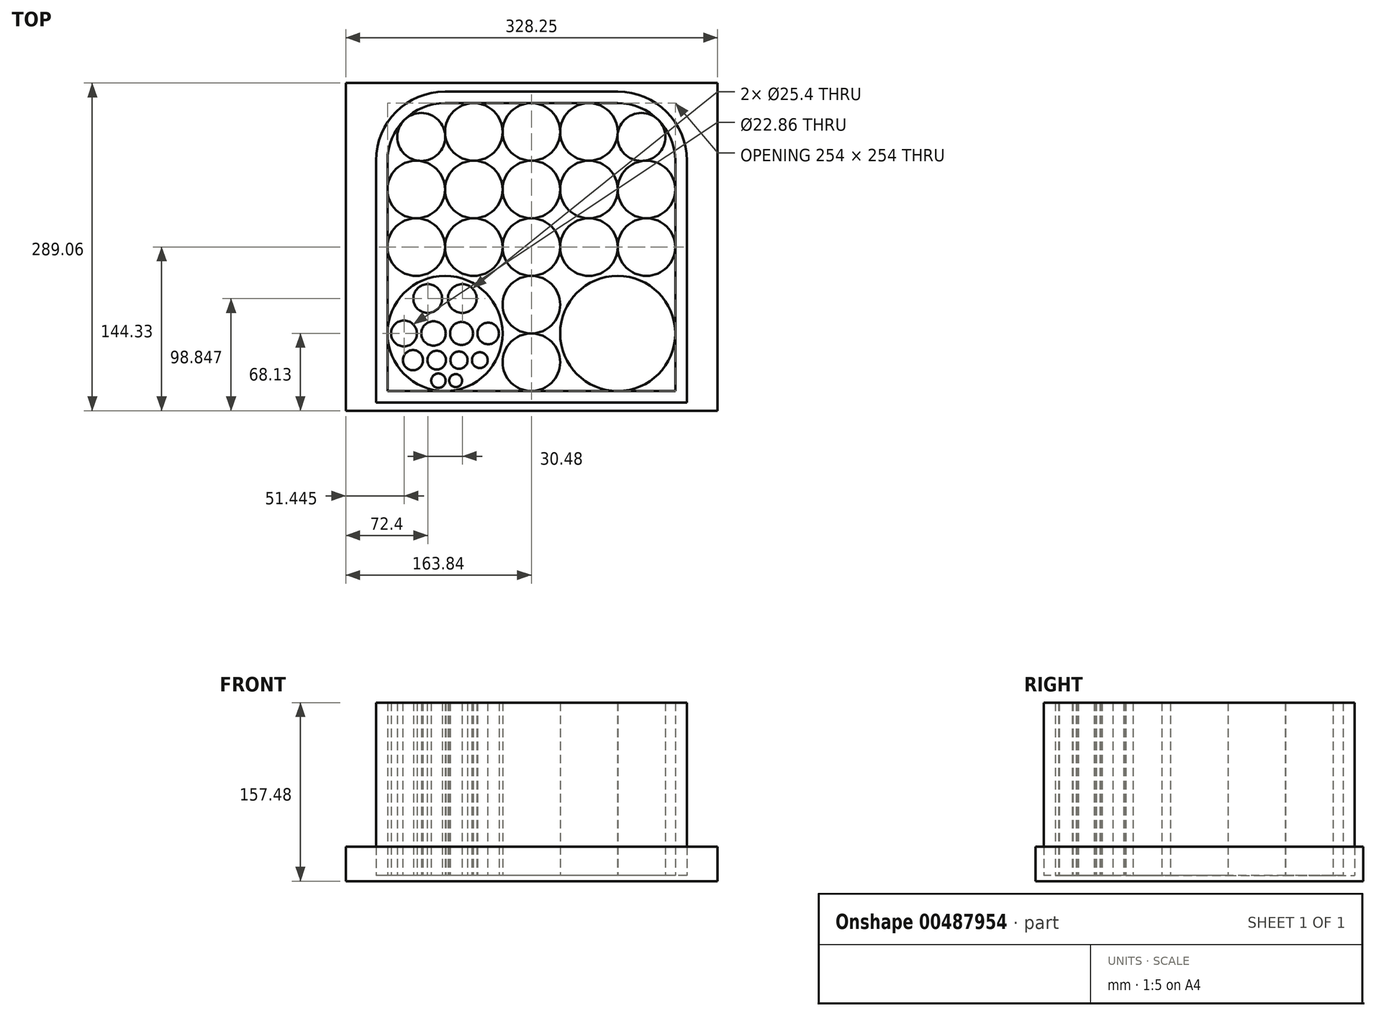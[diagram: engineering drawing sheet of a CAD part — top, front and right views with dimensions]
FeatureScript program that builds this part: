
annotation { "Feature Type Name" : "Feature", "Feature Type Description" : "" }
export const myFeature = defineFeature(function(context is Context, id is Id, definition is map)
    precondition{}
    {
        {
            var Q0;
            Q0=qCreatedBy(makeId("Top.planeOp"),FACE);
            var sketch = newSketch(context, id + "F0", { "sketchPlane" : qUnion([Q0])});
            skLineSegment(sketch, "E0.bottom", {"start": v(76.2, 127) * mm, "end": v(-76.2, 127) * mm});
            skLineSegment(sketch, "E0.top", {"start": v(127, -127) * mm, "end": v(-127, -127) * mm});
            skLineSegment(sketch, "E0.left", {"start": v(127, 76.2) * mm, "end": v(127, -127) * mm});
            skLineSegment(sketch, "E0.right", {"start": v(-127, 76.2) * mm, "end": v(-127, -127) * mm});
            skPoint(sketch, "E0.middle", {"position": v(0, 0) * mm});
            skCircle(sketch, "E1", {"center": v(-76.2, -76.2) * mm, "radius": 50.8 * mm});
            skCircle(sketch, "E2", {"center": v(76.2, -76.2) * mm, "radius": 50.8 * mm});
            skCircle(sketch, "E3", {"center": v(0, -101.6) * mm, "radius": 25.4 * mm});
            skCircle(sketch, "E4", {"center": v(0, -50.8) * mm, "radius": 25.4 * mm});
            skCircle(sketch, "E5", {"center": v(-101.6, 0) * mm, "radius": 25.4 * mm});
            skCircle(sketch, "E6", {"center": v(-50.8, 0) * mm, "radius": 25.4 * mm});
            skCircle(sketch, "E7", {"center": v(0, 0) * mm, "radius": 25.4 * mm});
            skCircle(sketch, "E8", {"center": v(50.8, 0) * mm, "radius": 25.4 * mm});
            skCircle(sketch, "E9", {"center": v(101.6, 0) * mm, "radius": 25.4 * mm});
            skPoint(sketch, "E10.visualSharp", {"position": v(-127, 127) * mm});
            skArc(sketch, "E10.filletArc", {"start": v(-76.2, 127) * mm, "mid": v(-112.12, 112.12) * mm, "end": v(-127, 76.2) * mm});
            skPoint(sketch, "E11.visualSharp", {"position": v(127, 127) * mm});
            skArc(sketch, "E11.filletArc", {"start": v(127, 76.2) * mm, "mid": v(112.12, 112.12) * mm, "end": v(76.2, 127) * mm});
            skCircle(sketch, "E12", {"center": v(-101.6, 50.8) * mm, "radius": 25.4 * mm});
            skCircle(sketch, "E13", {"center": v(-50.8, 50.8) * mm, "radius": 25.4 * mm});
            skCircle(sketch, "E14", {"center": v(0, 50.8) * mm, "radius": 25.4 * mm});
            skCircle(sketch, "E15", {"center": v(50.8, 50.8) * mm, "radius": 25.4 * mm});
            skCircle(sketch, "E16", {"center": v(101.6, 50.8) * mm, "radius": 25.4 * mm});
            skCircle(sketch, "E17", {"center": v(-50.8, 101.6) * mm, "radius": 25.4 * mm});
            skCircle(sketch, "E18", {"center": v(0, 101.6) * mm, "radius": 25.4 * mm});
            skCircle(sketch, "E19", {"center": v(50.8, 101.6) * mm, "radius": 25.4 * mm});
            skCircle(sketch, "E20", {"center": v(97.15, 97.15) * mm, "radius": 21.17 * mm});
            skCircle(sketch, "E21", {"center": v(-97.15, 97.15) * mm, "radius": 21.17 * mm});
            skArc(sketch, "E22.0", {"start": v(137.16, 76.2) * mm, "mid": v(119.3, 119.3) * mm, "end": v(76.2, 137.16) * mm});
            skArc(sketch, "E22.1", {"start": v(-76.2, 137.16) * mm, "mid": v(-119.3, 119.3) * mm, "end": v(-137.16, 76.2) * mm});
            skLineSegment(sketch, "E22.2", {"start": v(-137.16, 76.2) * mm, "end": v(-137.16, -137.16) * mm});
            skLineSegment(sketch, "E22.3", {"start": v(76.2, 137.16) * mm, "end": v(-76.2, 137.16) * mm});
            skLineSegment(sketch, "E22.4", {"start": v(137.16, -137.16) * mm, "end": v(-137.16, -137.16) * mm});
            skLineSegment(sketch, "E22.5", {"start": v(137.16, 76.2) * mm, "end": v(137.16, -137.16) * mm});
            skCircle(sketch, "E23", {"center": v(-91.44, -45.48) * mm, "radius": 12.7 * mm});
            skCircle(sketch, "E24", {"center": v(-60.96, -45.48) * mm, "radius": 12.7 * mm});
            skCircle(sketch, "E25", {"center": v(-112.4, -76.2) * mm, "radius": 11.43 * mm});
            skCircle(sketch, "E26", {"center": v(-86.36, -76.2) * mm, "radius": 10.8 * mm});
            skCircle(sketch, "E27", {"center": v(-61.6, -76.2) * mm, "radius": 10.16 * mm});
            skCircle(sketch, "E28", {"center": v(-38.1, -76.2) * mm, "radius": 9.53 * mm});
            skCircle(sketch, "E29", {"center": v(-104.5, -99.76) * mm, "radius": 8.9 * mm});
            skCircle(sketch, "E30", {"center": v(-83.55, -99.76) * mm, "radius": 8.26 * mm});
            skCircle(sketch, "E31", {"center": v(-63.87, -99.76) * mm, "radius": 7.62 * mm});
            skCircle(sketch, "E32", {"center": v(-45.45, -99.76) * mm, "radius": 6.99 * mm});
            skCircle(sketch, "E33", {"center": v(-82.06, -117.83) * mm, "radius": 6.35 * mm});
            skCircle(sketch, "E34", {"center": v(-66.82, -117.83) * mm, "radius": 5.72 * mm});
            skSolve(sketch);
        }
        {
            var Q0;
            {var subQ0=sQuery(id+"F0.wireOp",EDGE,"E12");var subQ1=makeQuery(id+"F0.imprint","INTERSECT",VERTEX,{"derivedFrom":[subQ0,sQuery(id+"F0.wireOp",EDGE,"E21")]});Q0=makeQuery(id+"F0.imprint","IMPRINT",FACE,{"disambiguationData":[TD([[makeQuery(id+"F0.imprint","IMPRINT",EDGE,{"disambiguationData":[TD([[subQ1,1.0]])],"derivedFrom":subQ0}),1.0]])]});}
            var Q1;
            {var subQ0=sQuery(id+"F0.wireOp",EDGE,"E13");var subQ1=makeQuery(id+"F0.imprint","INTERSECT",VERTEX,{"derivedFrom":[subQ0,sQuery(id+"F0.wireOp",EDGE,"E17")]});Q1=makeQuery(id+"F0.imprint","IMPRINT",FACE,{"disambiguationData":[TD([[makeQuery(id+"F0.imprint","IMPRINT",EDGE,{"disambiguationData":[TD([[subQ1,1.0]])],"derivedFrom":subQ0}),1.0]])]});}
            var Q2;
            {var subQ0=sQuery(id+"F0.wireOp",EDGE,"E14");var subQ1=makeQuery(id+"F0.imprint","INTERSECT",VERTEX,{"derivedFrom":[subQ0,sQuery(id+"F0.wireOp",EDGE,"E18")]});Q2=makeQuery(id+"F0.imprint","IMPRINT",FACE,{"disambiguationData":[TD([[makeQuery(id+"F0.imprint","IMPRINT",EDGE,{"disambiguationData":[TD([[subQ1,1.0]])],"derivedFrom":subQ0}),1.0]])]});}
            var Q3;
            {var subQ0=sQuery(id+"F0.wireOp",EDGE,"E7");var subQ1=makeQuery(id+"F0.imprint","INTERSECT",VERTEX,{"derivedFrom":[subQ0,sQuery(id+"F0.wireOp",EDGE,"E14")]});Q3=makeQuery(id+"F0.imprint","IMPRINT",FACE,{"disambiguationData":[TD([[makeQuery(id+"F0.imprint","IMPRINT",EDGE,{"disambiguationData":[TD([[subQ1,1.0]])],"derivedFrom":subQ0}),1.0]])]});}
            var Q4;
            {var subQ0=sQuery(id+"F0.wireOp",EDGE,"E6");var subQ1=makeQuery(id+"F0.imprint","INTERSECT",VERTEX,{"derivedFrom":[subQ0,sQuery(id+"F0.wireOp",EDGE,"E13")]});Q4=makeQuery(id+"F0.imprint","IMPRINT",FACE,{"disambiguationData":[TD([[makeQuery(id+"F0.imprint","IMPRINT",EDGE,{"disambiguationData":[TD([[subQ1,1.0]])],"derivedFrom":subQ0}),1.0]])]});}
            var Q5;
            {var subQ0=sQuery(id+"F0.wireOp",EDGE,"E5");var subQ1=makeQuery(id+"F0.imprint","INTERSECT",VERTEX,{"derivedFrom":[subQ0,sQuery(id+"F0.wireOp",EDGE,"E12")]});Q5=makeQuery(id+"F0.imprint","IMPRINT",FACE,{"disambiguationData":[TD([[makeQuery(id+"F0.imprint","IMPRINT",EDGE,{"disambiguationData":[TD([[subQ1,1.0]])],"derivedFrom":subQ0}),1.0]])]});}
            var Q6;
            {var subQ0=sQuery(id+"F0.wireOp",EDGE,"E21");var subQ1=makeQuery(id+"F0.imprint","INTERSECT",VERTEX,{"derivedFrom":[sQuery(id+"F0.wireOp",EDGE,"E10.filletArc"),subQ0]});Q6=makeQuery(id+"F0.imprint","IMPRINT",FACE,{"disambiguationData":[TD([[makeQuery(id+"F0.imprint","IMPRINT",EDGE,{"disambiguationData":[TD([[subQ1,1.0]])],"derivedFrom":subQ0}),1.0]])]});}
            var Q7;
            {var subQ0=sQuery(id+"F0.wireOp",EDGE,"E17");var subQ1=makeQuery(id+"F0.imprint","INTERSECT",VERTEX,{"derivedFrom":[sQuery(id+"F0.wireOp",EDGE,"E0.bottom"),subQ0]});Q7=makeQuery(id+"F0.imprint","IMPRINT",FACE,{"disambiguationData":[TD([[makeQuery(id+"F0.imprint","IMPRINT",EDGE,{"disambiguationData":[TD([[subQ1,1.0]])],"derivedFrom":subQ0}),1.0]])]});}
            var Q8;
            {var subQ0=sQuery(id+"F0.wireOp",EDGE,"E18");var subQ1=makeQuery(id+"F0.imprint","INTERSECT",VERTEX,{"derivedFrom":[sQuery(id+"F0.wireOp",EDGE,"E0.bottom"),subQ0]});Q8=makeQuery(id+"F0.imprint","IMPRINT",FACE,{"disambiguationData":[TD([[makeQuery(id+"F0.imprint","IMPRINT",EDGE,{"disambiguationData":[TD([[subQ1,1.0]])],"derivedFrom":subQ0}),1.0]])]});}
            var Q9;
            {var subQ0=sQuery(id+"F0.wireOp",EDGE,"E19");var subQ1=makeQuery(id+"F0.imprint","INTERSECT",VERTEX,{"derivedFrom":[sQuery(id+"F0.wireOp",EDGE,"E0.bottom"),subQ0]});Q9=makeQuery(id+"F0.imprint","IMPRINT",FACE,{"disambiguationData":[TD([[makeQuery(id+"F0.imprint","IMPRINT",EDGE,{"disambiguationData":[TD([[subQ1,-1.0]])],"derivedFrom":subQ0}),1.0]])]});}
            var Q10;
            {var subQ0=sQuery(id+"F0.wireOp",EDGE,"E20");var subQ1=makeQuery(id+"F0.imprint","INTERSECT",VERTEX,{"derivedFrom":[sQuery(id+"F0.wireOp",EDGE,"E11.filletArc"),subQ0]});Q10=makeQuery(id+"F0.imprint","IMPRINT",FACE,{"disambiguationData":[TD([[makeQuery(id+"F0.imprint","IMPRINT",EDGE,{"disambiguationData":[TD([[subQ1,-1.0]])],"derivedFrom":subQ0}),1.0]])]});}
            var Q11;
            {var subQ0=sQuery(id+"F0.wireOp",EDGE,"E15");var subQ1=makeQuery(id+"F0.imprint","INTERSECT",VERTEX,{"derivedFrom":[subQ0,sQuery(id+"F0.wireOp",EDGE,"E19")]});Q11=makeQuery(id+"F0.imprint","IMPRINT",FACE,{"disambiguationData":[TD([[makeQuery(id+"F0.imprint","IMPRINT",EDGE,{"disambiguationData":[TD([[subQ1,1.0]])],"derivedFrom":subQ0}),1.0]])]});}
            var Q12;
            {var subQ0=sQuery(id+"F0.wireOp",EDGE,"E16");var subQ1=makeQuery(id+"F0.imprint","INTERSECT",VERTEX,{"derivedFrom":[sQuery(id+"F0.wireOp",EDGE,"E0.left"),subQ0]});Q12=makeQuery(id+"F0.imprint","IMPRINT",FACE,{"disambiguationData":[TD([[makeQuery(id+"F0.imprint","IMPRINT",EDGE,{"disambiguationData":[TD([[subQ1,-1.0]])],"derivedFrom":subQ0}),1.0]])]});}
            var Q13;
            {var subQ0=sQuery(id+"F0.wireOp",EDGE,"E9");var subQ1=makeQuery(id+"F0.imprint","INTERSECT",VERTEX,{"derivedFrom":[sQuery(id+"F0.wireOp",EDGE,"E0.left"),subQ0]});Q13=makeQuery(id+"F0.imprint","IMPRINT",FACE,{"disambiguationData":[TD([[makeQuery(id+"F0.imprint","IMPRINT",EDGE,{"disambiguationData":[TD([[subQ1,-1.0]])],"derivedFrom":subQ0}),1.0]])]});}
            var Q14;
            {var subQ0=sQuery(id+"F0.wireOp",EDGE,"E8");var subQ1=makeQuery(id+"F0.imprint","INTERSECT",VERTEX,{"derivedFrom":[subQ0,sQuery(id+"F0.wireOp",EDGE,"E15")]});Q14=makeQuery(id+"F0.imprint","IMPRINT",FACE,{"disambiguationData":[TD([[makeQuery(id+"F0.imprint","IMPRINT",EDGE,{"disambiguationData":[TD([[subQ1,1.0]])],"derivedFrom":subQ0}),1.0]])]});}
            var Q15;
            {var subQ0=sQuery(id+"F0.wireOp",EDGE,"E2");var subQ1=makeQuery(id+"F0.imprint","INTERSECT",VERTEX,{"derivedFrom":[sQuery(id+"F0.wireOp",EDGE,"E0.top"),subQ0]});Q15=makeQuery(id+"F0.imprint","IMPRINT",FACE,{"disambiguationData":[TD([[makeQuery(id+"F0.imprint","IMPRINT",EDGE,{"disambiguationData":[TD([[subQ1,1.0]])],"derivedFrom":subQ0}),1.0]])]});}
            var Q16;
            {var subQ0=sQuery(id+"F0.wireOp",EDGE,"E3");var subQ1=makeQuery(id+"F0.imprint","INTERSECT",VERTEX,{"derivedFrom":[sQuery(id+"F0.wireOp",EDGE,"E0.top"),subQ0]});Q16=makeQuery(id+"F0.imprint","IMPRINT",FACE,{"disambiguationData":[TD([[makeQuery(id+"F0.imprint","IMPRINT",EDGE,{"disambiguationData":[TD([[subQ1,1.0]])],"derivedFrom":subQ0}),1.0]])]});}
            var Q17;
            {var subQ0=sQuery(id+"F0.wireOp",EDGE,"E1");var subQ1=makeQuery(id+"F0.imprint","INTERSECT",VERTEX,{"derivedFrom":[sQuery(id+"F0.wireOp",EDGE,"E0.top"),subQ0]});Q17=makeQuery(id+"F0.imprint","IMPRINT",FACE,{"disambiguationData":[TD([[makeQuery(id+"F0.imprint","IMPRINT",EDGE,{"disambiguationData":[TD([[subQ1,1.0]])],"derivedFrom":subQ0}),1.0]])]});}
            var Q18;
            {var subQ0=sQuery(id+"F0.wireOp",EDGE,"E4");var subQ1=makeQuery(id+"F0.imprint","INTERSECT",VERTEX,{"derivedFrom":[sQuery(id+"F0.wireOp",EDGE,"E3"),subQ0]});Q18=makeQuery(id+"F0.imprint","IMPRINT",FACE,{"disambiguationData":[TD([[makeQuery(id+"F0.imprint","IMPRINT",EDGE,{"disambiguationData":[TD([[subQ1,1.0]])],"derivedFrom":subQ0}),1.0]])]});}
            extrude(context, id + "F1", {"entities" : qUnion([Q0, Q1, Q2, Q3, Q4, Q5, Q6, Q7, Q8, Q9, Q10, Q11, Q12, Q13, Q14, Q15, Q16, Q17, Q18]), "depth" : 152.4 * mm});
        }
        {
            var Q0;
            Q0=makeQuery(id+"F0.imprint","IMPRINT",FACE,{"disambiguationData":[TD([[makeQuery(id+"F0.imprint","IMPRINT",EDGE,{"derivedFrom":sQuery(id+"F0.wireOp",EDGE,"E22.0")}),1.0]])]});
            extrude(context, id + "F2", {"entities" : qUnion([Q0]), "depth" : 152.4 * mm});
        }
        {
            var Q0;
            Q0=makeQuery(id+"F0.imprint","IMPRINT",FACE,{"disambiguationData":[TD([[makeQuery(id+"F0.imprint","IMPRINT",EDGE,{"derivedFrom":sQuery(id+"F0.wireOp",EDGE,"E22.0")}),1.0]])]});
            cPlane(context, id + "F3", {"entities" : qUnion([Q0]), "cplaneType" : CPlaneType.OFFSET, "offset" : 25.4 * mm, "width" : 152.4 * mm, "height" : 152.4 * mm});
        }
        {
            var Q0;
            Q0=qCreatedBy(id+"F3.planeOp",FACE);
            var sketch = newSketch(context, id + "F4", { "sketchPlane" : qUnion([Q0])});
            skLineSegment(sketch, "E35.bottom", {"start": v(-163.84, 144.73) * mm, "end": v(164.4, 144.73) * mm});
            skLineSegment(sketch, "E35.top", {"start": v(-163.84, -144.33) * mm, "end": v(164.4, -144.33) * mm});
            skLineSegment(sketch, "E35.left", {"start": v(-163.84, 144.73) * mm, "end": v(-163.84, -144.33) * mm});
            skLineSegment(sketch, "E35.right", {"start": v(164.4, 144.73) * mm, "end": v(164.4, -144.33) * mm});
            skSolve(sketch);
        }
        {
            var Q0;
            Q0=makeQuery(id+"F4.imprint","IMPRINT",FACE,{"disambiguationData":[TD([[makeQuery(id+"F4.imprint","IMPRINT",EDGE,{"derivedFrom":sQuery(id+"F4.wireOp",EDGE,"E35.bottom")}),-1.0]])]});
            extrude(context, id + "F5", {"entities" : qUnion([Q0]), "oppositeDirection" : true, "depth" : 30.48 * mm});
        }
    });
